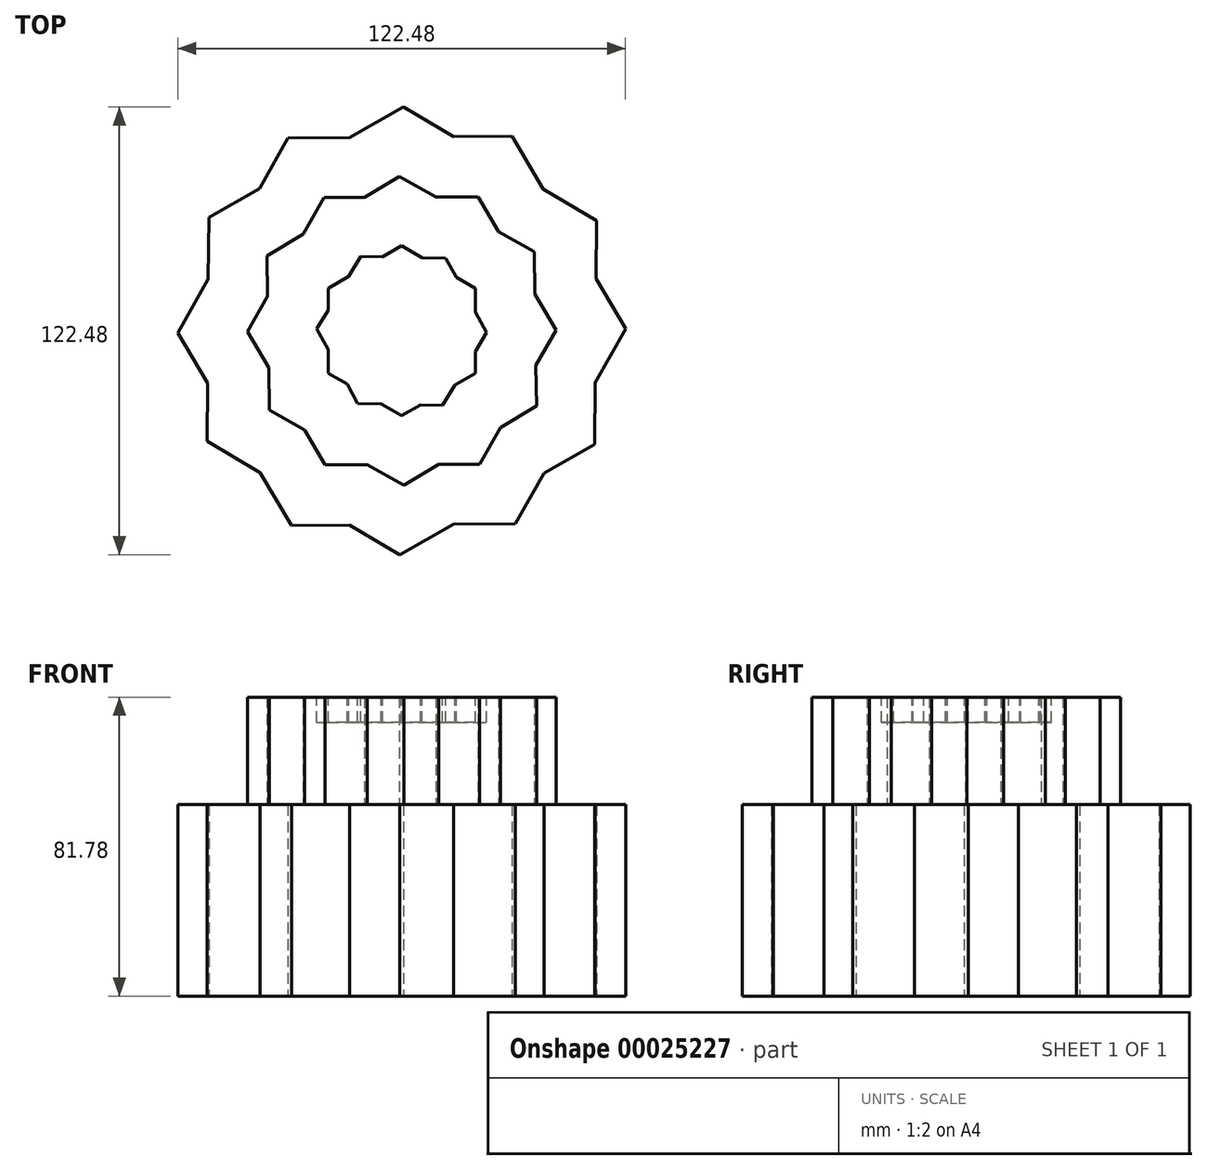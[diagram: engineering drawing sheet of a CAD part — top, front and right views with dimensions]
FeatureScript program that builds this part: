
annotation { "Feature Type Name" : "Feature", "Feature Type Description" : "" }
export const myFeature = defineFeature(function(context is Context, id is Id, definition is map)
    precondition{}
    {
        {
            var Q0;
            Q0=qCreatedBy(makeId("Top.planeOp"),FACE);
            var sketch = newSketch(context, id + "F0", { "sketchPlane" : qUnion([Q0])});
            skCircle(sketch, "E0.cCircle", {"center": v(0, 0) * mm, "radius": 53.04 * mm, "construction": true});
            skLineSegment(sketch, "E0.0", {"start": v(0.5, 61.24) * mm, "end": v(53.28, 30.2) * mm});
            skLineSegment(sketch, "E0.1", {"start": v(53.28, 30.2) * mm, "end": v(52.8, -31.05) * mm});
            skLineSegment(sketch, "E0.2", {"start": v(52.8, -31.05) * mm, "end": v(-0.5, -61.24) * mm});
            skLineSegment(sketch, "E0.3", {"start": v(-0.5, -61.24) * mm, "end": v(-53.28, -30.2) * mm});
            skLineSegment(sketch, "E0.4", {"start": v(-53.28, -30.2) * mm, "end": v(-52.8, 31.05) * mm});
            skLineSegment(sketch, "E0.5", {"start": v(-52.8, 31.05) * mm, "end": v(0.5, 61.24) * mm});
            skPoint(sketch, "E0.0.midPoint", {"position": v(26.89, 45.72) * mm});
            skLineSegment(sketch, "E1.0", {"start": v(30.15, 53.3) * mm, "end": v(61.24, 0.54) * mm});
            skLineSegment(sketch, "E1.1", {"start": v(61.24, 0.54) * mm, "end": v(31.1, -52.77) * mm});
            skLineSegment(sketch, "E1.2", {"start": v(31.1, -52.77) * mm, "end": v(-30.15, -53.3) * mm});
            skLineSegment(sketch, "E1.3", {"start": v(-30.15, -53.3) * mm, "end": v(-61.24, -0.54) * mm});
            skLineSegment(sketch, "E1.4", {"start": v(-61.24, -0.54) * mm, "end": v(-31.1, 52.77) * mm});
            skLineSegment(sketch, "E1.5", {"start": v(-31.1, 52.77) * mm, "end": v(30.15, 53.3) * mm});
            skPoint(sketch, "E1.0.midPoint", {"position": v(45.7, 26.92) * mm});
            skSolve(sketch);
        }
        {
            var Q0;
            Q0 = qSketchRegion(id + "F0", true);
            extrude(context, id + "F1", {"entities" : qUnion([Q0]), "depth" : 52.35 * mm});
        }
        {
            var Q0;
            Q0=makeQuery(id+"F1.opExtrude","CAP_FACE",FACE,{"disambiguationData":[OSD([sQuery(id+"F0.wireOp",EDGE,"E0.0"),sQuery(id+"F0.wireOp",EDGE,"E0.1"),sQuery(id+"F0.wireOp",EDGE,"E0.2"),sQuery(id+"F0.wireOp",EDGE,"E0.3"),sQuery(id+"F0.wireOp",EDGE,"E0.4"),sQuery(id+"F0.wireOp",EDGE,"E0.5"),sQuery(id+"F0.wireOp",EDGE,"E1.0"),sQuery(id+"F0.wireOp",EDGE,"E1.1"),sQuery(id+"F0.wireOp",EDGE,"E1.2"),sQuery(id+"F0.wireOp",EDGE,"E1.3"),sQuery(id+"F0.wireOp",EDGE,"E1.4"),sQuery(id+"F0.wireOp",EDGE,"E1.5")])],"isStart":false});
            var sketch = newSketch(context, id + "F2", { "sketchPlane" : qUnion([Q0])});
            skCircle(sketch, "E2.cCircle", {"center": v(0, 0) * mm, "radius": 36.57 * mm, "construction": true});
            skLineSegment(sketch, "E2.0", {"start": v(-0.65, 42.23) * mm, "end": v(36.24, 21.68) * mm});
            skLineSegment(sketch, "E2.1", {"start": v(36.24, 21.68) * mm, "end": v(36.9, -20.55) * mm});
            skLineSegment(sketch, "E2.2", {"start": v(36.9, -20.55) * mm, "end": v(0.65, -42.23) * mm});
            skLineSegment(sketch, "E2.3", {"start": v(0.65, -42.23) * mm, "end": v(-36.24, -21.68) * mm});
            skLineSegment(sketch, "E2.4", {"start": v(-36.24, -21.68) * mm, "end": v(-36.9, 20.55) * mm});
            skLineSegment(sketch, "E2.5", {"start": v(-36.9, 20.55) * mm, "end": v(-0.65, 42.23) * mm});
            skPoint(sketch, "E2.0.midPoint", {"position": v(17.8, 31.95) * mm});
            skLineSegment(sketch, "E3.0", {"start": v(20.96, 36.66) * mm, "end": v(42.23, 0.18) * mm});
            skLineSegment(sketch, "E3.1", {"start": v(42.23, 0.18) * mm, "end": v(21.27, -36.48) * mm});
            skLineSegment(sketch, "E3.2", {"start": v(21.27, -36.48) * mm, "end": v(-20.96, -36.66) * mm});
            skLineSegment(sketch, "E3.3", {"start": v(-20.96, -36.66) * mm, "end": v(-42.23, -0.18) * mm});
            skLineSegment(sketch, "E3.4", {"start": v(-42.23, -0.18) * mm, "end": v(-21.27, 36.48) * mm});
            skLineSegment(sketch, "E3.5", {"start": v(-21.27, 36.48) * mm, "end": v(20.96, 36.66) * mm});
            skPoint(sketch, "E3.0.midPoint", {"position": v(31.6, 18.42) * mm});
            skSolve(sketch);
        }
        {
            var Q0;
            Q0 = qSketchRegion(id + "F2", true);
            extrude(context, id + "F3", {"entities" : qUnion([Q0]), "operationType" : NewBodyOperationType.ADD, "depth" : 29.43 * mm});
        }
        {
            var Q0;
            Q0=makeQuery(id+"F3.opExtrude","CAP_FACE",FACE,{"disambiguationData":[OSD([sQuery(id+"F2.wireOp",EDGE,"E2.0"),sQuery(id+"F2.wireOp",EDGE,"E2.1"),sQuery(id+"F2.wireOp",EDGE,"E2.2"),sQuery(id+"F2.wireOp",EDGE,"E2.3"),sQuery(id+"F2.wireOp",EDGE,"E2.4"),sQuery(id+"F2.wireOp",EDGE,"E2.5"),sQuery(id+"F2.wireOp",EDGE,"E3.0"),sQuery(id+"F2.wireOp",EDGE,"E3.1"),sQuery(id+"F2.wireOp",EDGE,"E3.2"),sQuery(id+"F2.wireOp",EDGE,"E3.3"),sQuery(id+"F2.wireOp",EDGE,"E3.4"),sQuery(id+"F2.wireOp",EDGE,"E3.5")])],"isStart":false});
            var sketch = newSketch(context, id + "F4", { "sketchPlane" : qUnion([Q0])});
            skCircle(sketch, "E4.cCircle", {"center": v(0, 0) * mm, "radius": 20.13 * mm, "construction": true});
            skLineSegment(sketch, "E4.0", {"start": v(20.13, 11.62) * mm, "end": v(20.13, -11.62) * mm});
            skLineSegment(sketch, "E4.1", {"start": v(20.13, -11.62) * mm, "end": v(0, -23.25) * mm});
            skLineSegment(sketch, "E4.2", {"start": v(0, -23.25) * mm, "end": v(-20.13, -11.62) * mm});
            skLineSegment(sketch, "E4.3", {"start": v(-20.13, -11.62) * mm, "end": v(-20.13, 11.62) * mm});
            skLineSegment(sketch, "E4.4", {"start": v(-20.13, 11.62) * mm, "end": v(0, 23.25) * mm});
            skLineSegment(sketch, "E4.5", {"start": v(0, 23.25) * mm, "end": v(20.13, 11.62) * mm});
            skPoint(sketch, "E4.0.midPoint", {"position": v(20.13, 0) * mm});
            skLineSegment(sketch, "E5.0", {"start": v(12.07, 19.87) * mm, "end": v(23.24, -0.52) * mm});
            skLineSegment(sketch, "E5.1", {"start": v(23.24, -0.52) * mm, "end": v(11.17, -20.39) * mm});
            skLineSegment(sketch, "E5.2", {"start": v(11.17, -20.39) * mm, "end": v(-12.07, -19.87) * mm});
            skLineSegment(sketch, "E5.3", {"start": v(-12.07, -19.87) * mm, "end": v(-23.24, 0.52) * mm});
            skLineSegment(sketch, "E5.4", {"start": v(-23.24, 0.52) * mm, "end": v(-11.17, 20.39) * mm});
            skLineSegment(sketch, "E5.5", {"start": v(-11.17, 20.39) * mm, "end": v(12.07, 19.87) * mm});
            skPoint(sketch, "E5.0.midPoint", {"position": v(17.66, 9.67) * mm});
            skSolve(sketch);
        }
        {
            var Q0;
            Q0 = qSketchRegion(id + "F4", true);
            extrude(context, id + "F5", {"entities" : qUnion([Q0]), "operationType" : NewBodyOperationType.REMOVE, "oppositeDirection" : true, "depth" : 6.9 * mm});
        }
    });
